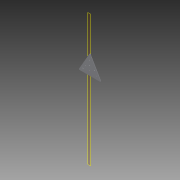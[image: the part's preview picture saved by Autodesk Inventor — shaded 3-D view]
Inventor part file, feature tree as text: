
AUTODESK INVENTOR PART (.ipt)
format: ipt  version: 2014 SP1 (Build 180222100, 222)  size: 100,352 bytes
history: native  units: in
note: dims shown in document units (in); Inventor stores cm internally (conversion verified against a paired STEP export)
features: reference x17, plane x1, extrude x1, fillet x1, sketch x1
ambient origin geometry x8: Origin, YZ Plane, XZ Plane, XY Plane, X Axis, Y Axis, Z Axis, Center Point
bodies: Solid1 (feature_tree)
feature tree (21):
  plane  "Work Plane1"
  extrude  "Extrusion1"  Depth=0.125in TaperAngle=0.0deg
  fillet  "Fillet1"  Radius=0.125in
  sketch  "Sketch1"  dims[d0=1.0in d1=0.125in d2=0.0in d3=0.125in]
  reference  "Reference1"
  reference  "Reference2"
  reference  "Reference3"
  reference  "Reference4"
  reference  "Reference5"
  reference  "Reference6"
  reference  "Reference7"
  reference  "Reference8"
  reference  "Reference9"
  reference  "Reference10"
  reference  "Reference11"
  reference  "Reference12"
  reference  "Reference13"
  reference  "Reference14"
  reference  "Reference15"
  reference  "Reference16"
  reference  "Reference17"
